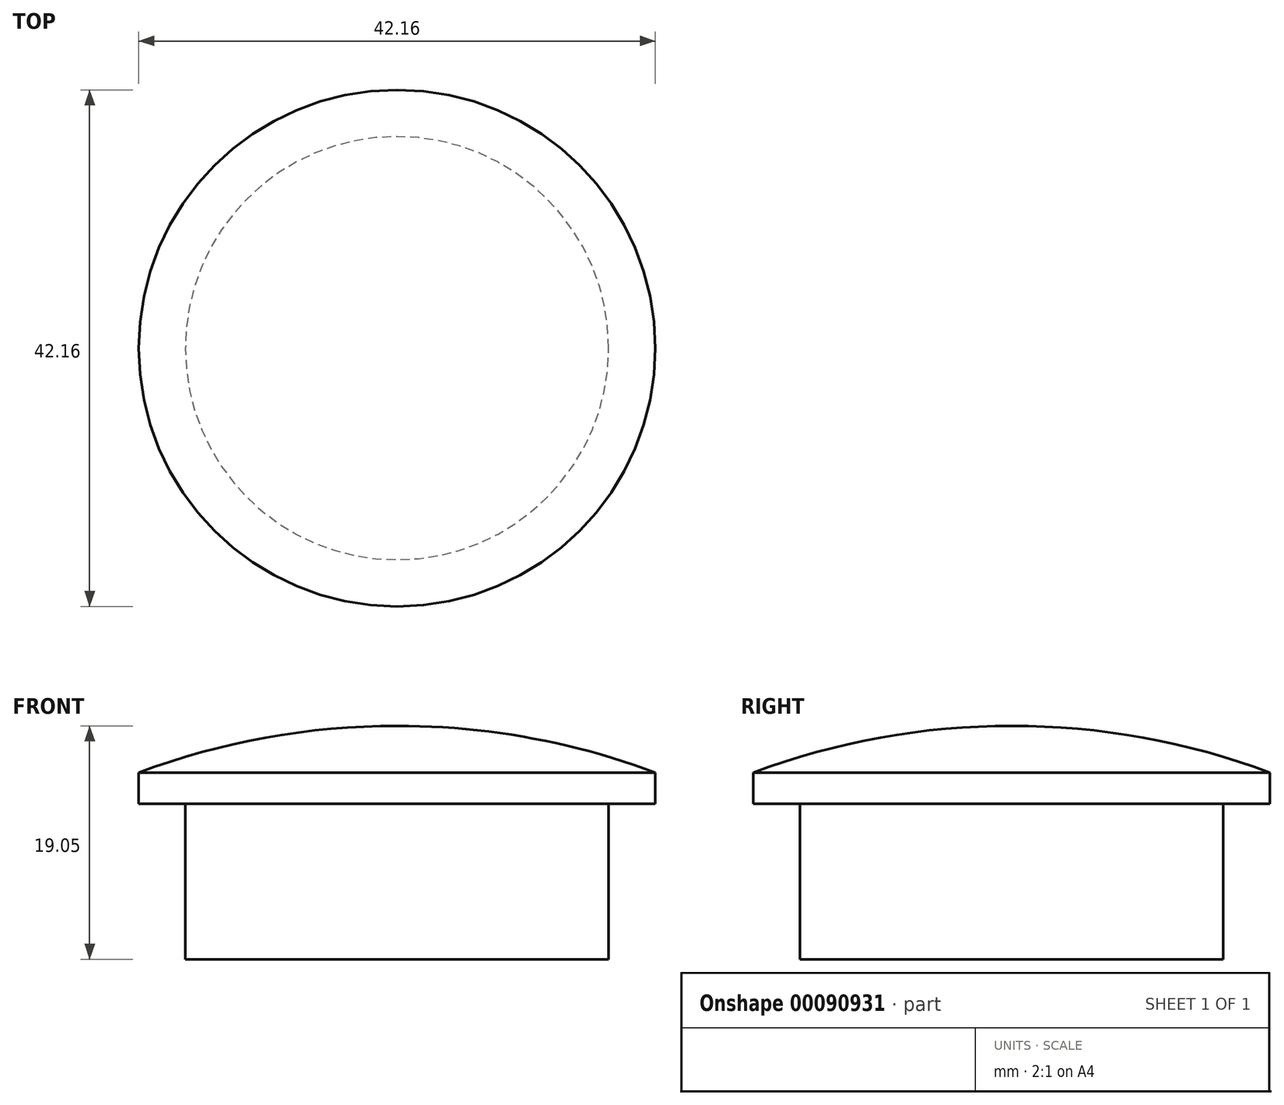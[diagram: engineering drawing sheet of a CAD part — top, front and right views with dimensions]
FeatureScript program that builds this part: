
annotation { "Feature Type Name" : "Feature", "Feature Type Description" : "" }
export const myFeature = defineFeature(function(context is Context, id is Id, definition is map)
    precondition{}
    {
        {
            var Q0;
            Q0=qCreatedBy(makeId("Front.planeOp"),FACE);
            var sketch = newSketch(context, id + "F0", { "sketchPlane" : qUnion([Q0])});
            skLineSegment(sketch, "E0", {"start": v(0, 0) * mm, "end": v(-17.27, 0) * mm});
            skLineSegment(sketch, "E1", {"start": v(-17.27, 0) * mm, "end": v(-17.27, 12.7) * mm});
            skLineSegment(sketch, "E2", {"start": v(-17.27, 12.7) * mm, "end": v(-21.08, 12.7) * mm});
            skLineSegment(sketch, "E3", {"start": v(-21.08, 12.7) * mm, "end": v(-21.08, 15.24) * mm});
            skLineSegment(sketch, "E4", {"start": v(-21.08, 15.24) * mm, "end": v(0, 15.24) * mm});
            skLineSegment(sketch, "E5", {"start": v(0, 15.24) * mm, "end": v(0, 0) * mm});
            skArc(sketch, "E6", {"start": v(0, 19.05) * mm, "mid": v(-10.71, 18.09) * mm, "end": v(-21.08, 15.24) * mm});
            skLineSegment(sketch, "E7", {"start": v(0, 19.05) * mm, "end": v(0, 15.24) * mm});
            skSolve(sketch);
        }
        {
            var Q0;
            Q0=makeQuery(id+"F0.imprint","IMPRINT",FACE,{"disambiguationData":[TD([[makeQuery(id+"F0.imprint","IMPRINT",EDGE,{"derivedFrom":sQuery(id+"F0.wireOp",EDGE,"E0")}),-1.0]])]});
            var Q1;
            Q1=makeQuery(id+"F0.imprint","IMPRINT",FACE,{"disambiguationData":[TD([[makeQuery(id+"F0.imprint","IMPRINT",EDGE,{"derivedFrom":sQuery(id+"F0.wireOp",EDGE,"E4")}),1.0]])]});
            var Q2;
            Q2=sQuery(id+"F0.wireOp",EDGE,"E5");
            revolve(context, id + "F1", {"entities" : qUnion([Q0, Q1]), "axis" : qUnion([Q2]), "revolveType" : RevolveType.FULL});
        }
    });
